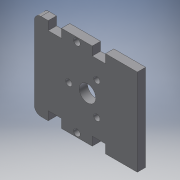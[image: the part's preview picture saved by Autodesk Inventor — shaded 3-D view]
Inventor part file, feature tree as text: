
AUTODESK INVENTOR PART (.ipt)
format: ipt  version: 2019 (Build 230136000, 136)  size: 151,552 bytes
history: native  units: in
note: dims shown in document units (in); Inventor stores cm internally (conversion verified against a paired STEP export)
features: reference x11, other x4, extrude x3, sketch x3, fillet x1, helix x1
ambient origin geometry x8: Origin, YZ Plane, XZ Plane, XY Plane, X Axis, Y Axis, Z Axis, Center Point
bodies: Solid1 (feature_tree)
feature tree (23):
  extrude  "Extrusion1"  Depth=0.1575in TaperAngle=0.0deg
  fillet  "Fillet1"  Radius=0.125in
  extrude  "Extrusion2"  Depth=0.0079in
  extrude  "Extrusion3"  Depth=0.1575in
  sketch  "Sketch1"  dims[d0=0.315in d1=0.1575in d2=0.0in d3=0.125in]
  reference  "Reference1"
  sketch  "Sketch2"  dims[d4=0.0079in d5=0.0079in]
  reference  "Reference2"
  reference  "Reference3"
  reference  "Reference4"
  reference  "Reference5"
  reference  "Reference6"
  reference  "Reference7"
  sketch  "Sketch3"  dims[d6=0.0079in d7=0.0079in d8=0.126in d9=0.126in d10=0.1575in d11=0.0in d12=0.1181in d13=1.1811in d15=360.0deg d17=0.1575in d18=0.0in]
  reference  "Reference8"
  reference  "Reference9"
  reference  "Reference10"
  reference  "Reference11"
  other  "<userpath>\Documents\CAD Files\Helix DLP\Helix DLP.iam"
  helix  "Helix DLP.iam"  [1 undecoded]
  other  "Z Motor Screw:1"
  other  "motor_brace_3:3"
  other  "motor_brace_3:4"
note: 1 required parameter value undecoded (feature->parameter linkage not recoverable at this tier; creation-order binding heuristic only, values carry confidence <= 0.55)
